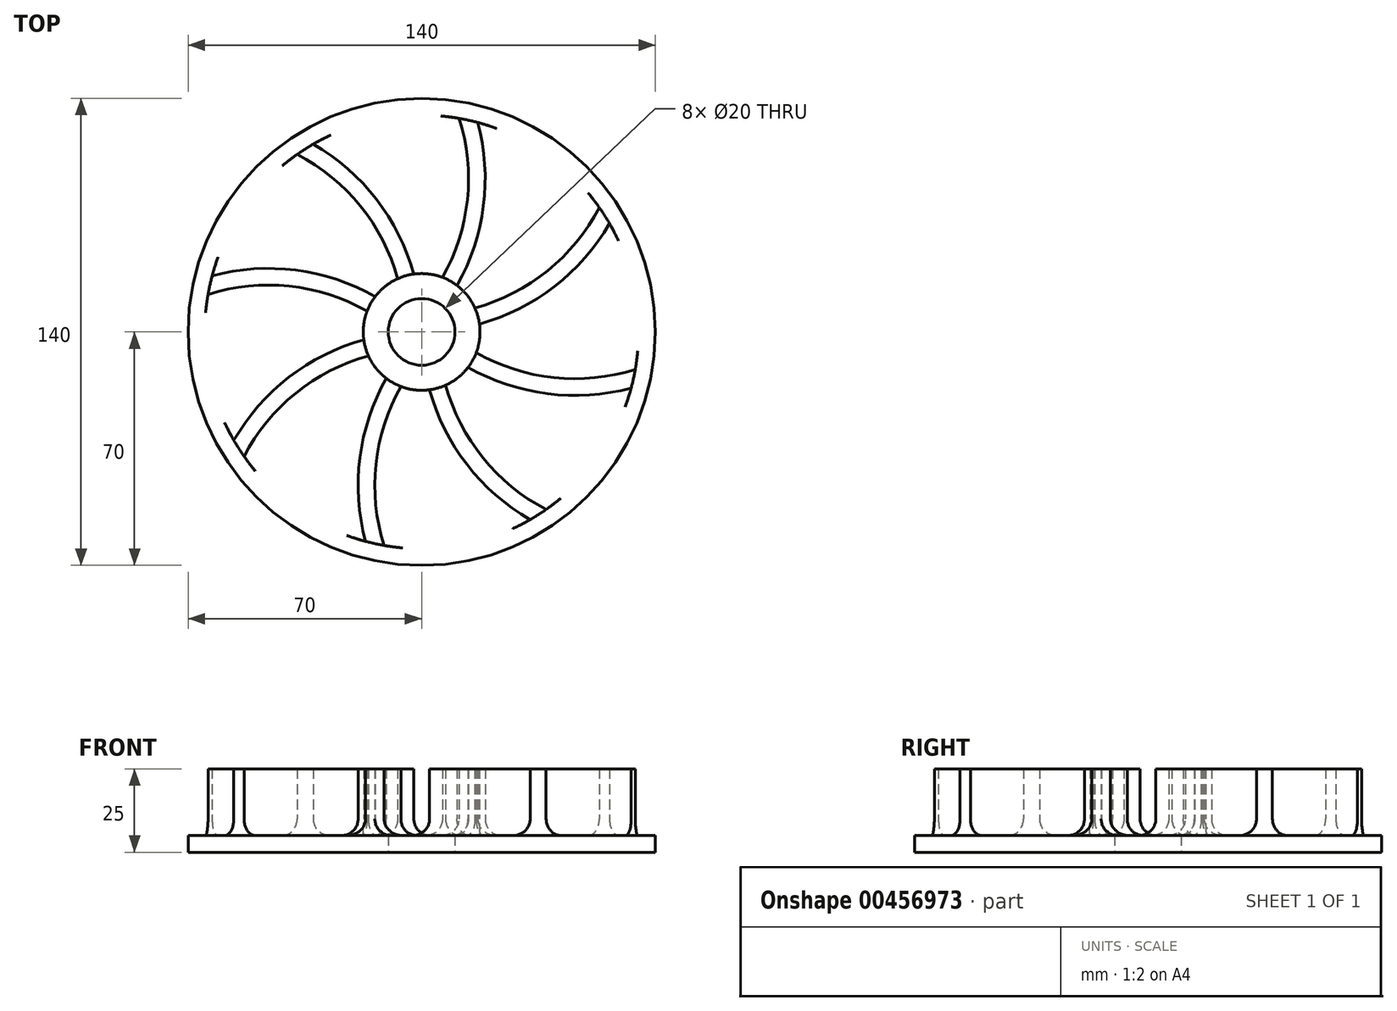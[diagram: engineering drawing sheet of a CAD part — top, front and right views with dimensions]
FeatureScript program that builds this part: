
annotation { "Feature Type Name" : "Feature", "Feature Type Description" : "" }
export const myFeature = defineFeature(function(context is Context, id is Id, definition is map)
    precondition{}
    {
        {
            var Q0;
            Q0=qCreatedBy(makeId("Top.planeOp"),FACE);
            var sketch = newSketch(context, id + "F0", { "sketchPlane" : qUnion([Q0])});
            skCircle(sketch, "E0", {"center": v(0, 0) * mm, "radius": 70 * mm});
            skCircle(sketch, "E1", {"center": v(0, 0) * mm, "radius": 10 * mm});
            skSolve(sketch);
        }
        {
            var Q0;
            Q0=makeQuery(id+"F0.imprint","IMPRINT",FACE,{"disambiguationData":[TD([[makeQuery(id+"F0.imprint","IMPRINT",EDGE,{"derivedFrom":sQuery(id+"F0.wireOp",EDGE,"E0")}),1.0]])]});
            var sketch = newSketch(context, id + "F1", { "sketchPlane" : qUnion([Q0])});
            skCircle(sketch, "E2", {"center": v(0, 0) * mm, "radius": 17.5 * mm});
            skCircle(sketch, "E3", {"center": v(0, 0) * mm, "radius": 65 * mm});
            skArc(sketch, "E4", {"start": v(-2.36, 17.34) * mm, "mid": v(-13.6, 39.78) * mm, "end": v(-32.5, 56.3) * mm});
            skArc(sketch, "E5.0", {"start": v(-7.16, 15.97) * mm, "mid": v(-18.35, 37.74) * mm, "end": v(-37.3, 53.23) * mm});
            skArc(sketch, "E6", {"start": v(-7.16, 15.97) * mm, "mid": v(-4.8, 16.83) * mm, "end": v(-2.36, 17.34) * mm});
            skArc(sketch, "E7", {"start": v(-37.3, 53.23) * mm, "mid": v(-34.94, 54.81) * mm, "end": v(-32.5, 56.3) * mm});
            skSolve(sketch);
        }
        {
            var Q0;
            {var subQ0=sQuery(id+"F1.wireOp",EDGE,"E4");Q0=makeQuery(id+"F1.imprint","IMPRINT",FACE,{"disambiguationData":[TD([[makeQuery(id+"F1.imprint","IMPRINT",EDGE,{"derivedFrom":subQ0}),1.0]])]});}
            extrude(context, id + "F2", {"entities" : qUnion([Q0]), "depth" : 25 * mm});
        }
        {
            var Q0;
            Q0 = qSketchRegion(id + "F0", true);
            extrude(context, id + "F3", {"entities" : qUnion([Q0]), "operationType" : NewBodyOperationType.ADD, "depth" : 5 * mm});
        }
        {
            var Q0;
            Q0=makeQuery(id+"F3.boolean.opBoolean","INTERSECT",EDGE,{"derivedFrom":[makeQuery(id+"F2.opExtrude","SWEPT_FACE",FACE,{"disambiguationData":[OSD([sQuery(id+"F1.wireOp",EDGE,"E4")])]}),makeQuery(id+"F3.opExtrude","CAP_FACE",FACE,{"disambiguationData":[OSD([sQuery(id+"F0.wireOp",EDGE,"E0"),sQuery(id+"F0.wireOp",EDGE,"E1")])],"isStart":false})]});
            var Q1;
            Q1=makeQuery(id+"F3.boolean.opBoolean","INTERSECT",EDGE,{"derivedFrom":[makeQuery(id+"F2.opExtrude","SWEPT_FACE",FACE,{"disambiguationData":[OSD([sQuery(id+"F1.wireOp",EDGE,"E5.0")])]}),makeQuery(id+"F3.opExtrude","CAP_FACE",FACE,{"disambiguationData":[OSD([sQuery(id+"F0.wireOp",EDGE,"E0"),sQuery(id+"F0.wireOp",EDGE,"E1")])],"isStart":false})]});
            fillet(context, id + "F4", {"entities" : qUnion([Q0, Q1]), "radius" : 5 * mm, "tangentPropagation" : true, "allowEdgeOverflow" : false});
        }
        {
            var Q0;
            Q0=makeQuery(id+"F2.opExtrude","SWEPT_BODY",BODY,{"disambiguationData":[OSD([sQuery(id+"F1.wireOp",EDGE,"E2"),sQuery(id+"F1.wireOp",EDGE,"E3"),sQuery(id+"F1.wireOp",EDGE,"E4"),sQuery(id+"F1.wireOp",EDGE,"E5.0")])]});
            var Q1;
            Q1=makeQuery(id+"F3.opExtrude","CAP_EDGE",EDGE,{"disambiguationData":[OSD([sQuery(id+"F0.wireOp",EDGE,"E1")])],"isStart":true});
            circularPattern(context, id + "F5", {"entities" : qUnion([Q0]), "axis" : qUnion([Q1]), "angle" : 360 * degree, "instanceCount" : 8, "equalSpace" : true});
        }
    });
